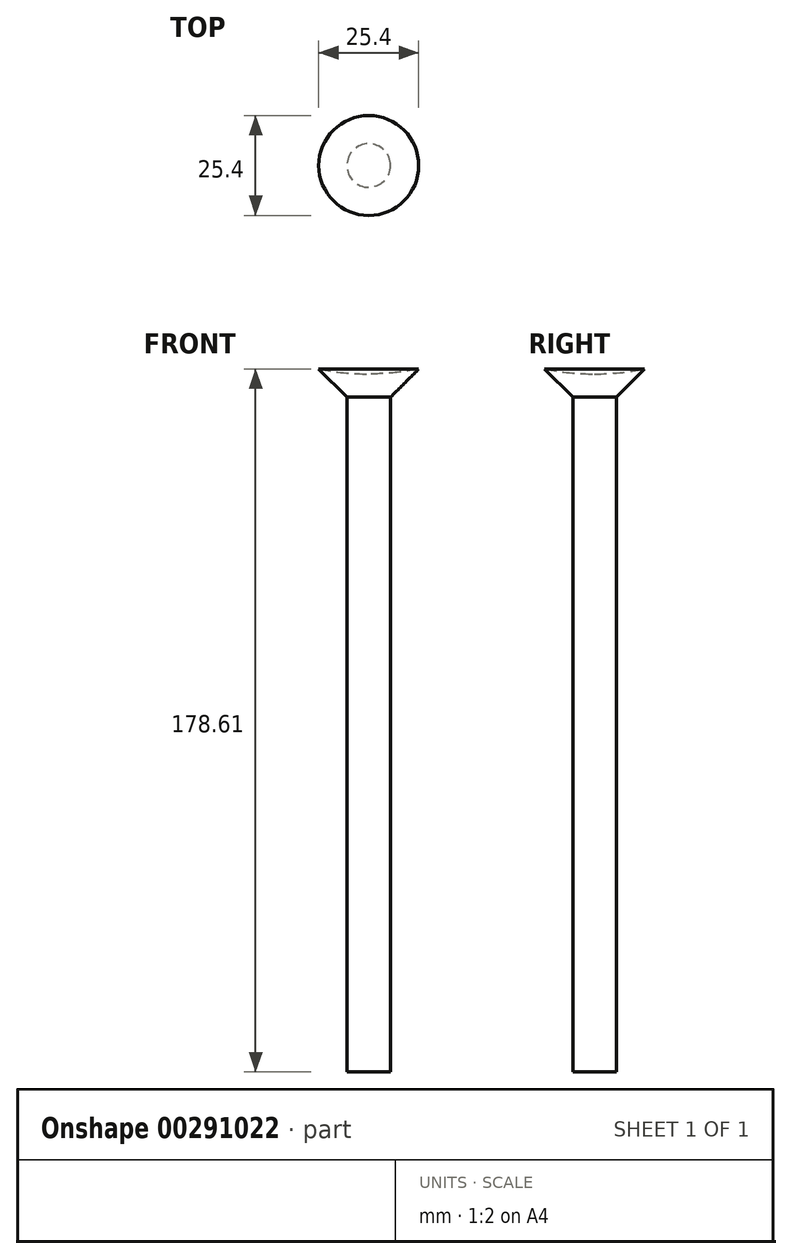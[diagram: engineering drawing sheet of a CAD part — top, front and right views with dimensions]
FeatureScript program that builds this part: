
annotation { "Feature Type Name" : "Feature", "Feature Type Description" : "" }
export const myFeature = defineFeature(function(context is Context, id is Id, definition is map)
    precondition{}
    {
        {
            var Q0;
            Q0=qCreatedBy(makeId("Top.planeOp"),FACE);
            var sketch = newSketch(context, id + "F0", { "sketchPlane" : qUnion([Q0])});
            skCircle(sketch, "E0", {"center": v(0, 0) * mm, "radius": 5.54 * mm});
            skSolve(sketch);
        }
        {
            var Q0;
            Q0=makeQuery(id+"F0.imprint","IMPRINT",FACE,{"disambiguationData":[TD([[makeQuery(id+"F0.imprint","IMPRINT",EDGE,{"derivedFrom":sQuery(id+"F0.wireOp",EDGE,"E0")}),1.0]])]});
            extrude(context, id + "F1", {"entities" : qUnion([Q0]), "depth" : 44.45 * mm});
        }
        {
            var Q0;
            Q0=makeQuery(id+"F1.opExtrude","CAP_FACE",FACE,{"disambiguationData":[OSD([sQuery(id+"F0.wireOp",EDGE,"E0")])],"isStart":false});
            var sketch = newSketch(context, id + "F2", { "sketchPlane" : qUnion([Q0])});
            skCircle(sketch, "E1", {"center": v(0, 0) * mm, "radius": 5.54 * mm});
            skSolve(sketch);
        }
        {
            var Q0;
            Q0=qSketchRegion(id+"F2",true);
            extrude(context, id + "F3", {"entities" : qUnion([Q0]), "operationType" : NewBodyOperationType.ADD, "depth" : 127 * mm});
        }
        {
            var Q0;
            Q0=makeQuery(id+"F3.opExtrude","CAP_FACE",FACE,{"disambiguationData":[OSD([sQuery(id+"F2.wireOp",EDGE,"E1")])],"isStart":false});
            var sketch = newSketch(context, id + "F4", { "sketchPlane" : qUnion([Q0])});
            skLineSegment(sketch, "E2", {"start": v(-5.54, 0) * mm, "end": v(5.54, 0) * mm});
            skSolve(sketch);
        }
        {
            var Q0;
            Q0=qCreatedBy(makeId("Front.planeOp"),FACE);
            var sketch = newSketch(context, id + "F5", { "sketchPlane" : qUnion([Q0])});
            skLineSegment(sketch, "E3", {"start": v(0, 178.61) * mm, "end": v(0, 171.45) * mm});
            skLineSegment(sketch, "E4", {"start": v(0, 171.45) * mm, "end": v(5.54, 171.45) * mm});
            skLineSegment(sketch, "E5", {"start": v(5.54, 171.45) * mm, "end": v(12.7, 178.61) * mm});
            skLineSegment(sketch, "E6", {"start": v(12.7, 178.61) * mm, "end": v(0, 178.61) * mm});
            skLineSegment(sketch, "E7.MirrorCS", {"start": v(-12.7, 178.61) * mm, "end": v(0, 178.61) * mm});
            skArc(sketch, "E8", {"start": v(0, 177.34) * mm, "mid": v(6.38, 305.3) * mm, "end": v(-12.7, 178.61) * mm});
            skLineSegment(sketch, "E9", {"start": v(0, 171.45) * mm, "end": v(0, 182.96) * mm, "construction": true});
            skSolve(sketch);
        }
        {
            var Q0;
            {var subQ0=sQuery(id+"F5.wireOp",EDGE,"E4");Q0=makeQuery(id+"F5.imprint","IMPRINT",FACE,{"disambiguationData":[TD([[makeQuery(id+"F5.imprint","IMPRINT",EDGE,{"derivedFrom":subQ0}),1.0]])]});}
            var Q1;
            Q1=sQuery(id+"F5.wireOp",EDGE,"E5");
            var Q2;
            Q2=sQuery(id+"F5.wireOp",EDGE,"E9");
            revolve(context, id + "F6", {"operationType" : NewBodyOperationType.ADD, "entities" : qUnion([Q0]), "surfaceEntities" : qUnion([Q1]), "axis" : qUnion([Q2]), "revolveType" : RevolveType.FULL});
        }
    });
